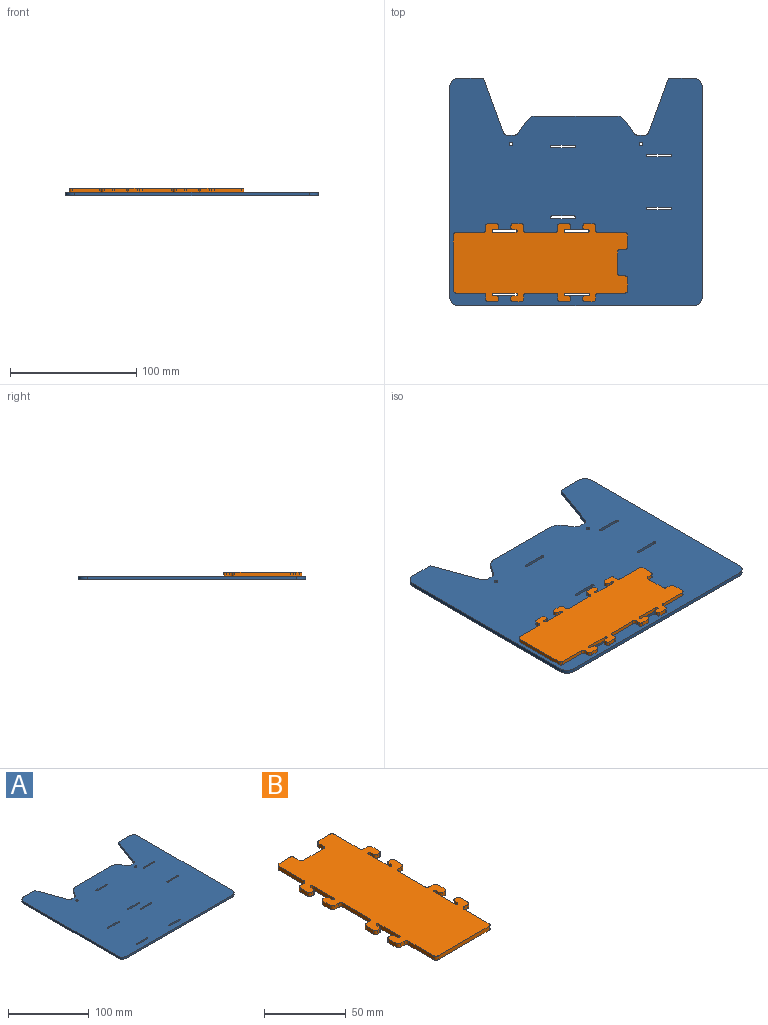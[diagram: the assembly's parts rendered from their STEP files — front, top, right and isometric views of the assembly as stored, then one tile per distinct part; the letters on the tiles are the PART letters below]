
ASSEMBLY  parts=2 mates=1
PART A: 58 faces, bbox 200x180x3 mm
  f0: plane 9.27x6.25mm, normal (0.83,0.56,0), area 33.5mm2, adj f1,f55,f56,f57
  f1: cylinder r=9mm len=7.46mm, axis (0,0,-1), area 26.4mm2, adj f0,f2,f56,f57
  f2: plane 63.87x3mm, normal (0,1,0), area 191.6mm2, adj f1,f3,f56,f57
  f3: cylinder r=9mm len=7.46mm, axis (0,0,-1), area 26.4mm2, adj f2,f4,f56,f57
  f4: plane 9.27x6.25mm, normal (-0.83,0.56,0), area 33.5mm2, adj f3,f5,f56,f57
  f5: cylinder r=4mm len=3.32mm, axis (0,0,-1), area 11.7mm2, adj f4,f6,f56,f57
  f6: plane 5.07x3mm, normal (0,1,0), area 15.2mm2, adj f5,f7,f56,f57
  f7: cylinder r=4mm len=3.76mm, axis (0,0,-1), area 14.7mm2, adj f6,f8,f56,f57
  f8: plane 42.37x15.42mm, normal (0.94,0.34,0), area 135.3mm2, adj f7,f9,f56,f57
  f9: plane 19.78x3mm, normal (0,1,0), area 59.4mm2, adj f8,f10,f56,f57
  f10: cylinder r=7mm len=7mm, axis (0,0,-1), area 33mm2, adj f9,f11,f56,f57
  f11: plane 166x3mm, normal (-1,0,0), area 498mm2, adj f10,f12,f56,f57
  f12: cylinder r=7mm len=7mm, axis (0,0,-1), area 33mm2, adj f11,f13,f56,f57
  f13: plane 186x3mm, normal (0,-1,0), area 558mm2, adj f12,f14,f56,f57
  f14: cylinder r=7mm len=7mm, axis (0,0,-1), area 33mm2, adj f13,f15,f56,f57
  f15: plane 166x3mm, normal (1,0,0), area 498mm2, adj f14,f16,f56,f57
  f16: cylinder r=7mm len=7mm, axis (0,0,-1), area 33mm2, adj f15,f17,f56,f57
  f17: plane 19.78x3mm, normal (0,1,0), area 59.4mm2, adj f16,f18,f56,f57
  f18: plane 42.37x15.42mm, normal (-0.94,0.34,0), area 135.3mm2, adj f17,f19,f56,f57
  f19: cylinder r=4mm len=3.76mm, axis (0,0,-1), area 14.7mm2, adj f18,f20,f56,f57
  f20: plane 5.07x3mm, normal (0,1,0), area 15.2mm2, adj f19,f55,f56,f57
  f21: cylinder r=1mm len=3mm, axis (0,0,-1), area 9.4mm2, adj f22,f45,f56,f57
  f22: plane 18x3mm, normal (0,1,0), area 54mm2, adj f21,f23,f56,f57
  f23: cylinder r=1mm len=3mm, axis (0,0,-1), area 9.4mm2, adj f22,f45,f56,f57
  f24: plane 18x3mm, normal (0,1,0), area 54mm2, adj f25,f46,f56,f57
  f25: cylinder r=1mm len=3mm, axis (0,0,-1), area 9.4mm2, adj f24,f26,f56,f57
  f26: plane 18x3mm, normal (0,-1,0), area 54mm2, adj f25,f46,f56,f57
  f27: cylinder r=1mm len=3mm, axis (0,0,-1), area 9.4mm2, adj f28,f49,f56,f57
  f28: plane 18x3mm, normal (0,-1,0), area 54mm2, adj f27,f29,f56,f57
  f29: cylinder r=1mm len=3mm, axis (0,0,-1), area 9.4mm2, adj f28,f49,f56,f57
  f30: cylinder r=1mm len=3mm, axis (0,0,-1), area 9.4mm2, adj f31,f50,f56,f57
  f31: plane 18x3mm, normal (0,-1,0), area 54mm2, adj f30,f32,f56,f57
  f32: cylinder r=1mm len=3mm, axis (0,0,-1), area 9.4mm2, adj f31,f50,f56,f57
  f33: cylinder r=1mm len=3mm, axis (0,0,-1), area 9.4mm2, adj f34,f51,f56,f57
  f34: plane 18x3mm, normal (0,-1,0), area 54mm2, adj f33,f35,f56,f57
  f35: cylinder r=1mm len=3mm, axis (0,0,-1), area 9.4mm2, adj f34,f51,f56,f57
  f36: cylinder r=1mm len=3mm, axis (0,0,-1), area 9.4mm2, adj f37,f52,f56,f57
  f37: plane 18x3mm, normal (0,-1,0), area 54mm2, adj f36,f38,f56,f57
  f38: cylinder r=1mm len=3mm, axis (0,0,-1), area 9.4mm2, adj f37,f52,f56,f57
  f39: cylinder r=1mm len=3mm, axis (0,0,-1), area 9.4mm2, adj f40,f53,f56,f57
  f40: plane 18x3mm, normal (0,-1,0), area 54mm2, adj f39,f41,f56,f57
  f41: cylinder r=1mm len=3mm, axis (0,0,-1), area 9.4mm2, adj f40,f53,f56,f57
  f42: cylinder r=1mm len=3mm, axis (0,0,-1), area 9.4mm2, adj f43,f54,f56,f57
  f43: plane 18x3mm, normal (0,-1,0), area 54mm2, adj f42,f44,f56,f57
  f44: cylinder r=1mm len=3mm, axis (0,0,-1), area 9.4mm2, adj f43,f54,f56,f57
  f45: plane 18x3mm, normal (0,-1,0), area 54mm2, adj f21,f23,f56,f57
  f46: cylinder r=1mm len=3mm, axis (0,0,-1), area 9.4mm2, adj f24,f26,f56,f57
  f47: cylinder r=1.5mm len=3mm, axis (0,0,-1), area 28.3mm2, adj f56,f57
  f48: cylinder r=1.5mm len=3mm, axis (0,0,-1), area 28.3mm2, adj f56,f57
  f49: plane 18x3mm, normal (0,1,0), area 54mm2, adj f27,f29,f56,f57
  f50: plane 18x3mm, normal (0,1,0), area 54mm2, adj f30,f32,f56,f57
  f51: plane 18x3mm, normal (0,1,0), area 54mm2, adj f33,f35,f56,f57
  f52: plane 18x3mm, normal (0,1,0), area 54mm2, adj f36,f38,f56,f57
  f53: plane 18x3mm, normal (0,1,0), area 54mm2, adj f39,f41,f56,f57
  f54: plane 18x3mm, normal (0,1,0), area 54mm2, adj f42,f44,f56,f57
  f55: cylinder r=4mm len=3.32mm, axis (0,0,-1), area 11.7mm2, adj f0,f20,f56,f57
  f56: plane 200x180mm, normal (0,0,1), area 31028.9mm2, adj f0,f1,f2,f3,f4,f5,f6,f7
  f57: plane 200x180mm, normal (0,0,-1), area 31028.9mm2, adj f0,f1,f2,f3,f4,f5,f6,f7
PART B: 98 faces, bbox 62x138x3 mm
  f0: cylinder r=1mm len=3mm, axis (0,0,-1), area 9.4mm2, adj f1,f95,f96,f97
  f1: plane 18x3mm, normal (1,0,0), area 54mm2, adj f0,f2,f96,f97
  f2: cylinder r=1mm len=3mm, axis (0,0,-1), area 9.4mm2, adj f1,f3,f96,f97
  f3: plane 3x2.5mm, normal (-1,0,0), area 7.5mm2, adj f2,f4,f96,f97
  f4: cylinder r=1.5mm len=3mm, axis (0,0,-1), area 7.1mm2, adj f3,f5,f96,f97
  f5: plane 3x2mm, normal (0,-1,0), area 6mm2, adj f4,f6,f96,f97
  f6: cylinder r=1.5mm len=3mm, axis (0,0,-1), area 7.1mm2, adj f5,f7,f96,f97
  f7: plane 6.5x3mm, normal (1,0,0), area 19.5mm2, adj f6,f8,f96,f97
  f8: cylinder r=2mm len=3mm, axis (0,0,-1), area 9.4mm2, adj f7,f9,f96,f97
  f9: plane 3x3mm, normal (0,1,0), area 9mm2, adj f8,f10,f96,f97
  f10: cylinder r=2mm len=3mm, axis (0,0,-1), area 9.4mm2, adj f9,f11,f96,f97
  f11: plane 23x3mm, normal (1,0,0), area 69mm2, adj f10,f12,f96,f97
  f12: cylinder r=2mm len=3mm, axis (0,0,-1), area 9.4mm2, adj f11,f13,f96,f97
  f13: plane 3x3mm, normal (0,-1,0), area 9mm2, adj f12,f14,f96,f97
  f14: cylinder r=2mm len=3mm, axis (0,0,-1), area 9.4mm2, adj f13,f15,f96,f97
  f15: plane 6.5x3mm, normal (1,0,0), area 19.5mm2, adj f14,f16,f96,f97
  f16: cylinder r=1.5mm len=3mm, axis (0,0,-1), area 7.1mm2, adj f15,f17,f96,f97
  f17: plane 3x2mm, normal (0,1,0), area 6mm2, adj f16,f18,f96,f97
  f18: cylinder r=1.5mm len=3mm, axis (0,0,-1), area 7.1mm2, adj f17,f19,f96,f97
  f19: plane 3x2.5mm, normal (-1,0,0), area 7.5mm2, adj f18,f20,f96,f97
  f20: cylinder r=1mm len=3mm, axis (0,0,-1), area 9.4mm2, adj f19,f21,f96,f97
  f21: plane 18x3mm, normal (1,0,0), area 54mm2, adj f20,f22,f96,f97
  f22: cylinder r=1mm len=3mm, axis (0,0,-1), area 9.4mm2, adj f21,f23,f96,f97
  f23: plane 3x2.5mm, normal (-1,0,0), area 7.5mm2, adj f22,f24,f96,f97
  f24: cylinder r=1.5mm len=3mm, axis (0,0,-1), area 7.1mm2, adj f23,f25,f96,f97
  f25: plane 3x2mm, normal (0,-1,0), area 6mm2, adj f24,f26,f96,f97
  f26: cylinder r=1.5mm len=3mm, axis (0,0,-1), area 7.1mm2, adj f25,f27,f96,f97
  f27: plane 6.5x3mm, normal (1,0,0), area 19.5mm2, adj f26,f28,f96,f97
  f28: cylinder r=2mm len=3mm, axis (0,0,-1), area 9.4mm2, adj f27,f29,f96,f97
  f29: plane 3x3mm, normal (0,1,0), area 9mm2, adj f28,f30,f96,f97
  f30: cylinder r=2mm len=3mm, axis (0,0,-1), area 9.4mm2, adj f29,f31,f96,f97
  f31: plane 21.5x3mm, normal (1,0,0), area 64.5mm2, adj f30,f32,f96,f97
  f32: cylinder r=2mm len=3mm, axis (0,0,-1), area 9.4mm2, adj f31,f33,f96,f97
  f33: plane 9.5x3mm, normal (0,1,0), area 28.5mm2, adj f32,f34,f96,f97
  f34: cylinder r=2mm len=3mm, axis (0,0,-1), area 9.4mm2, adj f33,f35,f96,f97
  f35: plane 4x3mm, normal (-1,0,0), area 12mm2, adj f34,f36,f96,f97
  f36: cylinder r=2mm len=3mm, axis (0,0,-1), area 9.4mm2, adj f35,f37,f96,f97
  f37: plane 17x3mm, normal (0,1,0), area 51mm2, adj f36,f38,f96,f97
  f38: cylinder r=2mm len=3mm, axis (0,0,-1), area 9.4mm2, adj f37,f39,f96,f97
  f39: plane 4x3mm, normal (1,0,0), area 12mm2, adj f38,f40,f96,f97
  f40: cylinder r=2mm len=3mm, axis (0,0,-1), area 9.4mm2, adj f39,f41,f96,f97
  f41: plane 9.5x3mm, normal (0,1,0), area 28.5mm2, adj f40,f42,f96,f97
  f42: cylinder r=2mm len=3mm, axis (0,0,-1), area 9.4mm2, adj f41,f43,f96,f97
  f43: plane 21.5x3mm, normal (-1,0,0), area 64.5mm2, adj f42,f44,f96,f97
  f44: cylinder r=2mm len=3mm, axis (0,0,-1), area 9.4mm2, adj f43,f45,f96,f97
  f45: plane 3x3mm, normal (0,1,0), area 9mm2, adj f44,f46,f96,f97
  f46: cylinder r=2mm len=3mm, axis (0,0,-1), area 9.4mm2, adj f45,f47,f96,f97
  f47: plane 6.5x3mm, normal (-1,0,0), area 19.5mm2, adj f46,f48,f96,f97
  f48: cylinder r=1.5mm len=3mm, axis (0,0,-1), area 7.1mm2, adj f47,f49,f96,f97
  f49: plane 3x2mm, normal (0,-1,0), area 6mm2, adj f48,f50,f96,f97
  f50: cylinder r=1.5mm len=3mm, axis (0,0,-1), area 7.1mm2, adj f49,f51,f96,f97
  f51: plane 3x2.5mm, normal (1,0,0), area 7.5mm2, adj f50,f52,f96,f97
  f52: cylinder r=1mm len=3mm, axis (0,0,-1), area 9.4mm2, adj f51,f53,f96,f97
  f53: plane 18x3mm, normal (-1,0,0), area 54mm2, adj f52,f54,f96,f97
  f54: cylinder r=1mm len=3mm, axis (0,0,-1), area 9.4mm2, adj f53,f55,f96,f97
  f55: plane 3x2.5mm, normal (1,0,0), area 7.5mm2, adj f54,f56,f96,f97
  f56: cylinder r=1.5mm len=3mm, axis (0,0,-1), area 7.1mm2, adj f55,f57,f96,f97
  f57: plane 3x2mm, normal (0,1,0), area 6mm2, adj f56,f58,f96,f97
  f58: cylinder r=1.5mm len=3mm, axis (0,0,-1), area 7.1mm2, adj f57,f59,f96,f97
  f59: plane 6.5x3mm, normal (-1,0,0), area 19.5mm2, adj f58,f60,f96,f97
  f60: cylinder r=2mm len=3mm, axis (0,0,-1), area 9.4mm2, adj f59,f61,f96,f97
  f61: plane 3x3mm, normal (0,-1,0), area 9mm2, adj f60,f62,f96,f97
  f62: cylinder r=2mm len=3mm, axis (0,0,-1), area 9.4mm2, adj f61,f63,f96,f97
  f63: plane 23x3mm, normal (-1,0,0), area 69mm2, adj f62,f64,f96,f97
  f64: cylinder r=2mm len=3mm, axis (0,0,-1), area 9.4mm2, adj f63,f65,f96,f97
  f65: plane 3x3mm, normal (0,1,0), area 9mm2, adj f64,f66,f96,f97
  f66: cylinder r=2mm len=3mm, axis (0,0,-1), area 9.4mm2, adj f65,f67,f96,f97
  f67: plane 6.5x3mm, normal (-1,0,0), area 19.5mm2, adj f66,f68,f96,f97
  f68: cylinder r=1.5mm len=3mm, axis (0,0,-1), area 7.1mm2, adj f67,f69,f96,f97
  f69: plane 3x2mm, normal (0,-1,0), area 6mm2, adj f68,f70,f96,f97
  f70: cylinder r=1.5mm len=3mm, axis (0,0,-1), area 7.1mm2, adj f69,f71,f96,f97
  f71: plane 3x2.5mm, normal (1,0,0), area 7.5mm2, adj f70,f72,f96,f97
  f72: cylinder r=1mm len=3mm, axis (0,0,-1), area 9.4mm2, adj f71,f73,f96,f97
  f73: plane 18x3mm, normal (-1,0,0), area 54mm2, adj f72,f74,f96,f97
  f74: cylinder r=1mm len=3mm, axis (0,0,-1), area 9.4mm2, adj f73,f75,f96,f97
  f75: plane 3x2.5mm, normal (1,0,0), area 7.5mm2, adj f74,f76,f96,f97
  f76: cylinder r=1.5mm len=3mm, axis (0,0,-1), area 7.1mm2, adj f75,f77,f96,f97
  f77: plane 3x2mm, normal (0,1,0), area 6mm2, adj f76,f78,f96,f97
  f78: cylinder r=1.5mm len=3mm, axis (0,0,-1), area 7.1mm2, adj f77,f79,f96,f97
  f79: plane 6.5x3mm, normal (-1,0,0), area 19.5mm2, adj f78,f80,f96,f97
  f80: cylinder r=2mm len=3mm, axis (0,0,-1), area 9.4mm2, adj f79,f81,f96,f97
  f81: plane 3x3mm, normal (0,-1,0), area 9mm2, adj f80,f82,f96,f97
  f82: cylinder r=2mm len=3mm, axis (0,0,-1), area 9.4mm2, adj f81,f83,f96,f97
  f83: plane 21.5x3mm, normal (-1,0,0), area 64.5mm2, adj f82,f84,f96,f97
  f84: cylinder r=2mm len=3mm, axis (0,0,-1), area 9.4mm2, adj f83,f85,f96,f97
  f85: plane 44x3mm, normal (0,-1,0), area 132mm2, adj f84,f86,f96,f97
  f86: cylinder r=2mm len=3mm, axis (0,0,-1), area 9.4mm2, adj f85,f87,f96,f97
  f87: plane 21.5x3mm, normal (1,0,0), area 64.5mm2, adj f86,f88,f96,f97
  f88: cylinder r=2mm len=3mm, axis (0,0,-1), area 9.4mm2, adj f87,f89,f96,f97
  f89: plane 3x3mm, normal (0,-1,0), area 9mm2, adj f88,f90,f96,f97
  f90: cylinder r=2mm len=3mm, axis (0,0,-1), area 9.4mm2, adj f89,f91,f96,f97
  f91: plane 6.5x3mm, normal (1,0,0), area 19.5mm2, adj f90,f92,f96,f97
  f92: cylinder r=1.5mm len=3mm, axis (0,0,-1), area 7.1mm2, adj f91,f93,f96,f97
  f93: plane 3x2mm, normal (0,1,0), area 6mm2, adj f92,f94,f96,f97
  f94: cylinder r=1.5mm len=3mm, axis (0,0,-1), area 7.1mm2, adj f93,f95,f96,f97
  f95: plane 3x2.5mm, normal (-1,0,0), area 7.5mm2, adj f0,f94,f96,f97
  f96: plane 138x62mm, normal (0,0,1), area 6928.3mm2, adj f0,f1,f2,f3,f4,f5,f6,f7
  f97: plane 138x62mm, normal (0,0,-1), area 6928.3mm2, adj f0,f1,f2,f3,f4,f5,f6,f7
PLACE A t=(-7,-7,-3)mm
PLACE B rot(axis=(0,0,-1),90deg) t=(-4,51,0)mm
MATE fastened A.f30 <-> B.f0  axis (0,0,1) through (27.5,2,0)mm
